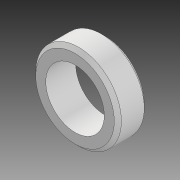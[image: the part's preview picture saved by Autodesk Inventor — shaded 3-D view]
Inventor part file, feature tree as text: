
AUTODESK INVENTOR PART (.ipt)
format: ipt  version: 2020 (Build 240168000, 168)  size: 100,352 bytes
history: native  units: mm
features: extrude x1, chamfer x1, sketch x1
ambient origin geometry x8: Origin, YZ Plane, XZ Plane, XY Plane, X Axis, Y Axis, Z Axis, Center Point
bodies: Solid1 (feature_tree)
feature tree (3):
  extrude  "Extrusion1"  Depth=4.2mm
  chamfer  "Chamfer1"  Distance=4.2mm
  sketch  "Sketch1"  dims[d0=8.2mm d1=12.0mm d2=4.2mm d3=0.0mm d4=0.5mm d5=2.0mm d6=45.0deg]
